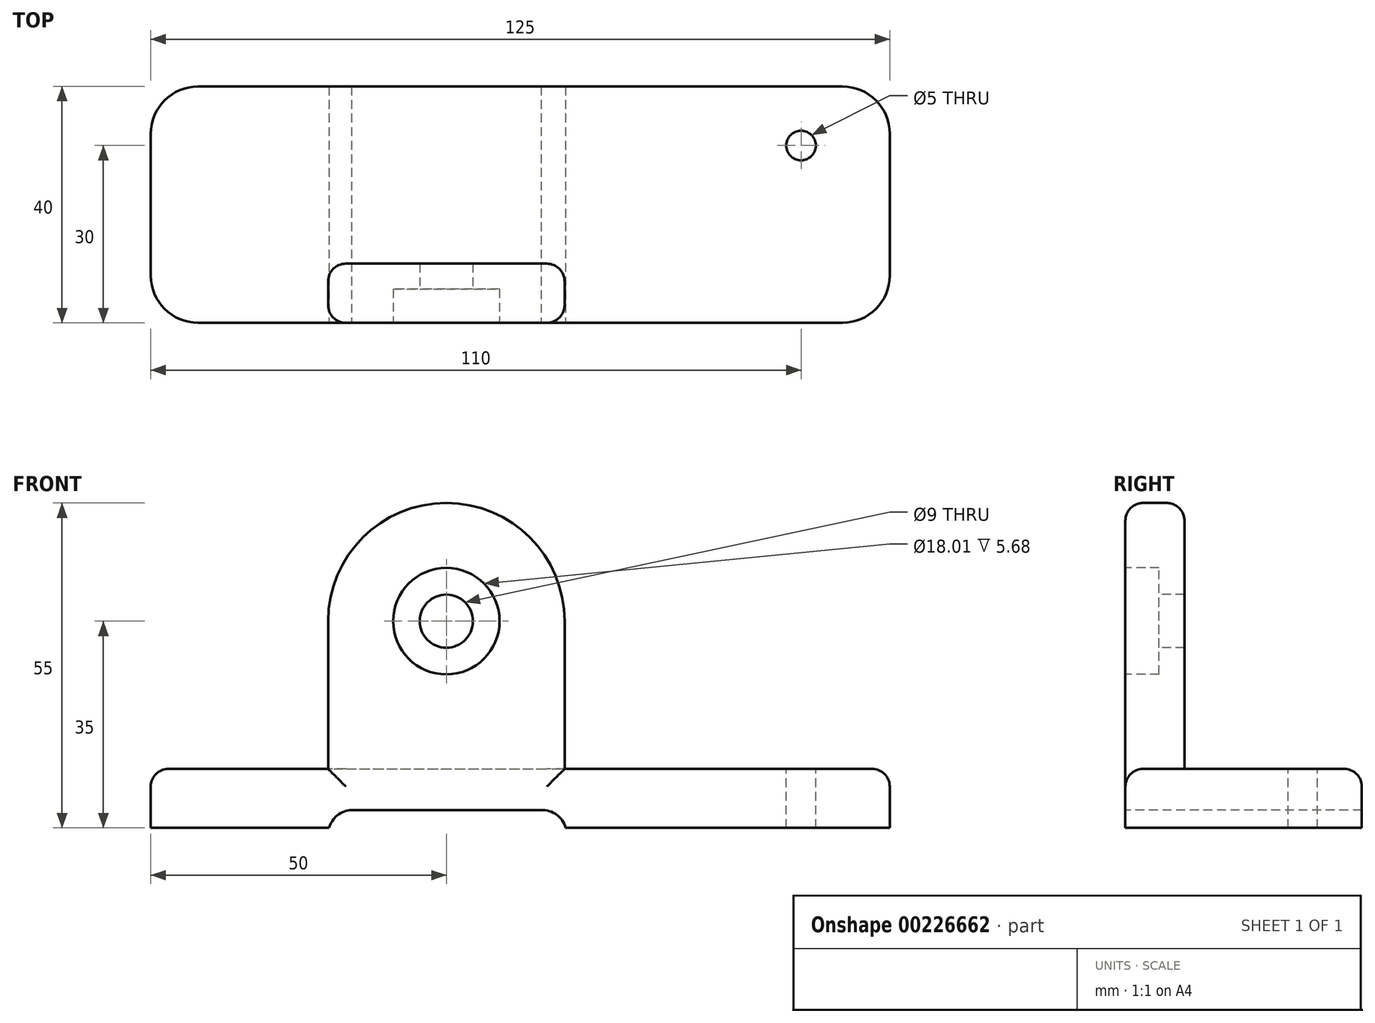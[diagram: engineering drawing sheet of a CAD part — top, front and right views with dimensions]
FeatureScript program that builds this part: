
annotation { "Feature Type Name" : "Feature", "Feature Type Description" : "" }
export const myFeature = defineFeature(function(context is Context, id is Id, definition is map)
    precondition{}
    {
        {
            var Q0;
            Q0=qCreatedBy(makeId("Top.planeOp"),FACE);
            var sketch = newSketch(context, id + "F0", { "sketchPlane" : qUnion([Q0])});
            skLineSegment(sketch, "E0.bottom", {"start": v(-62.5, 20) * mm, "end": v(62.5, 20) * mm});
            skLineSegment(sketch, "E0.top", {"start": v(-62.5, -20) * mm, "end": v(62.5, -20) * mm});
            skLineSegment(sketch, "E0.left", {"start": v(-62.5, 20) * mm, "end": v(-62.5, -20) * mm});
            skLineSegment(sketch, "E0.right", {"start": v(62.5, 20) * mm, "end": v(62.5, -20) * mm});
            skPoint(sketch, "E0.middle", {"position": v(0, 0) * mm});
            skSolve(sketch);
        }
        {
            var Q0;
            Q0=makeQuery(id+"F0.imprint","IMPRINT",FACE,{"disambiguationData":[TD([[makeQuery(id+"F0.imprint","IMPRINT",EDGE,{"derivedFrom":sQuery(id+"F0.wireOp",EDGE,"E0.bottom")}),-1.0]])]});
            extrude(context, id + "F1", {"entities" : qUnion([Q0]), "oppositeDirection" : true, "depth" : 10 * mm});
        }
        {
            var Q0;
            Q0=makeQuery(id+"F1.opExtrude","CAP_FACE",FACE,{"disambiguationData":[OSD([sQuery(id+"F0.wireOp",EDGE,"E0.bottom"),sQuery(id+"F0.wireOp",EDGE,"E0.top"),sQuery(id+"F0.wireOp",EDGE,"E0.left"),sQuery(id+"F0.wireOp",EDGE,"E0.right")])],"isStart":true});
            var sketch = newSketch(context, id + "F2", { "sketchPlane" : qUnion([Q0])});
            skLineSegment(sketch, "E1.bottom", {"start": v(-32.5, -20) * mm, "end": v(7.5, -20) * mm});
            skLineSegment(sketch, "E1.top", {"start": v(-32.5, -10) * mm, "end": v(7.5, -10) * mm});
            skLineSegment(sketch, "E1.left", {"start": v(-32.5, -20) * mm, "end": v(-32.5, -10) * mm});
            skLineSegment(sketch, "E1.right", {"start": v(7.5, -20) * mm, "end": v(7.5, -10) * mm});
            skSolve(sketch);
        }
        {
            var Q0;
            Q0 = qSketchRegion(id + "F2", true);
            extrude(context, id + "F3", {"entities" : qUnion([Q0]), "operationType" : NewBodyOperationType.ADD, "depth" : 25 * mm});
        }
        {
            var Q0;
            Q0=makeQuery(id+"F3.boolean.opBoolean","MERGE",FACE,{"derivedFrom":[makeQuery(id+"F1.opExtrude","SWEPT_FACE",FACE,{"disambiguationData":[OSD([sQuery(id+"F0.wireOp",EDGE,"E0.top")])]}),makeQuery(id+"F3.opExtrude","SWEPT_FACE",FACE,{"disambiguationData":[OSD([sQuery(id+"F2.wireOp",EDGE,"E1.bottom")])]})]});
            var sketch = newSketch(context, id + "F4", { "sketchPlane" : qUnion([Q0])});
            skArc(sketch, "E2", {"start": v(7.5, 25) * mm, "mid": v(-12.5, 45) * mm, "end": v(-32.5, 25) * mm});
            skSolve(sketch);
        }
        {
            var Q0;
            Q0 = qSketchRegion(id + "F4", true);
            var Q1;
            Q1=makeQuery(id+"F4.imprint","IMPRINT",FACE,{"disambiguationData":[TD([[makeQuery(id+"F4.imprint","IMPRINT",EDGE,{"derivedFrom":sQuery(id+"F4.wireOp",EDGE,"E2")}),1.0]])]});
            extrude(context, id + "F5", {"entities" : qUnion([Q0, Q1]), "operationType" : NewBodyOperationType.ADD, "oppositeDirection" : true, "depth" : 10 * mm});
        }
        {
            var Q0;
            {var subQ0=sQuery(id+"F2.wireOp",EDGE,"E1.bottom");Q0=makeQuery(id+"F5.boolean.opBoolean","MERGE",FACE,{"derivedFrom":[makeQuery(id+"F3.boolean.opBoolean","MERGE",FACE,{"derivedFrom":[makeQuery(id+"F1.opExtrude","SWEPT_FACE",FACE,{"disambiguationData":[OSD([sQuery(id+"F0.wireOp",EDGE,"E0.top")])]}),makeQuery(id+"F3.opExtrude","SWEPT_FACE",FACE,{"disambiguationData":[OSD([subQ0])]})]}),makeQuery(id+"F5.opExtrude","CAP_FACE",FACE,{"disambiguationData":[OSD([subQ0,sQuery(id+"F4.wireOp",EDGE,"E2")])],"isStart":true})]});}
            var sketch = newSketch(context, id + "F6", { "sketchPlane" : qUnion([Q0])});
            skCircle(sketch, "E3", {"center": v(-12.5, 25) * mm, "radius": 9 * mm});
            skSolve(sketch);
        }
        {
            var Q0;
            Q0=sQuery(id+"F6.wireOp",VERTEX,"E3.center");
            var Q1;
            Q1=makeQuery(id+"F1.opExtrude","SWEPT_BODY",BODY,{"disambiguationData":[OSD([sQuery(id+"F0.wireOp",EDGE,"E0.bottom"),sQuery(id+"F0.wireOp",EDGE,"E0.top"),sQuery(id+"F0.wireOp",EDGE,"E0.left"),sQuery(id+"F0.wireOp",EDGE,"E0.right")])]});
            hole(context, id + "F7", {"style" : HoleStyle.C_BORE, "endStyle" : HoleEndStyle.THROUGH, "holeDiameter" : 9 * mm, "cBoreDiameter" : 18.01 * mm, "cBoreDepth" : 5.68 * mm, "locations" : qUnion([Q0]), "scope" : qUnion([Q1]), "isTappedThrough" : true});
        }
        {
            var Q0;
            {var subQ0=sQuery(id+"F2.wireOp",EDGE,"E1.bottom");Q0=makeQuery(id+"F5.boolean.opBoolean","MERGE",FACE,{"derivedFrom":[makeQuery(id+"F3.boolean.opBoolean","MERGE",FACE,{"derivedFrom":[makeQuery(id+"F1.opExtrude","SWEPT_FACE",FACE,{"disambiguationData":[OSD([sQuery(id+"F0.wireOp",EDGE,"E0.top")])]}),makeQuery(id+"F3.opExtrude","SWEPT_FACE",FACE,{"disambiguationData":[OSD([subQ0])]})]}),makeQuery(id+"F5.opExtrude","CAP_FACE",FACE,{"disambiguationData":[OSD([subQ0,sQuery(id+"F4.wireOp",EDGE,"E2")])],"isStart":true})]});}
            var sketch = newSketch(context, id + "F8", { "sketchPlane" : qUnion([Q0])});
            skLineSegment(sketch, "E4", {"start": v(-32.33, -10) * mm, "end": v(11.28, -10) * mm, "construction": true});
            skArc(sketch, "E5", {"start": v(-28.55, -7) * mm, "mid": v(-30.94, -7.87) * mm, "end": v(-32.33, -10) * mm});
            skLineSegment(sketch, "E6", {"start": v(11.28, -10) * mm, "end": v(11.28, -10) * mm});
            skLineSegment(sketch, "E7", {"start": v(-28.55, -7) * mm, "end": v(-28.55, -10) * mm, "construction": true});
            skLineSegment(sketch, "E8", {"start": v(3.55, -10) * mm, "end": v(3.55, -7) * mm, "construction": true});
            skArc(sketch, "E9", {"start": v(7.67, -10) * mm, "mid": v(6.15, -7.76) * mm, "end": v(3.55, -7) * mm});
            skLineSegment(sketch, "E10", {"start": v(-28.55, -7) * mm, "end": v(3.55, -7) * mm});
            skPoint(sketch, "E11", {"position": v(-12.5, -7) * mm});
            skSolve(sketch);
        }
        {
            var Q0;
            {var subQ0=sQuery(id+"F8.wireOp",EDGE,"E5");Q0=makeQuery(id+"F8.imprint","IMPRINT",FACE,{"disambiguationData":[TD([[makeQuery(id+"F8.imprint","IMPRINT",EDGE,{"derivedFrom":subQ0}),1.0]])]});}
            extrude(context, id + "F9", {"entities" : qUnion([Q0]), "operationType" : NewBodyOperationType.REMOVE, "endBound" : BoundingType.THROUGH_ALL, "oppositeDirection" : true, "depth" : 25 * mm});
        }
        {
            var Q0;
            Q0=makeQuery(id+"F1.opExtrude","CAP_FACE",FACE,{"disambiguationData":[OSD([sQuery(id+"F0.wireOp",EDGE,"E0.bottom"),sQuery(id+"F0.wireOp",EDGE,"E0.top"),sQuery(id+"F0.wireOp",EDGE,"E0.left"),sQuery(id+"F0.wireOp",EDGE,"E0.right")])],"isStart":true});
            var sketch = newSketch(context, id + "F10", { "sketchPlane" : qUnion([Q0])});
            skCircle(sketch, "E12", {"center": v(47.5, 10) * mm, "radius": 2.5 * mm});
            skSolve(sketch);
        }
        {
            var Q0;
            Q0=makeQuery(id+"F10.imprint","IMPRINT",FACE,{"disambiguationData":[TD([[makeQuery(id+"F10.imprint","IMPRINT",EDGE,{"derivedFrom":sQuery(id+"F10.wireOp",EDGE,"E12")}),1.0]])]});
            extrude(context, id + "F11", {"entities" : qUnion([Q0]), "operationType" : NewBodyOperationType.REMOVE, "endBound" : BoundingType.THROUGH_ALL, "oppositeDirection" : true, "depth" : 25 * mm});
        }
        {
            var Q0;
            Q0=makeQuery(id+"F3.opExtrude","SWEPT_EDGE",EDGE,{"disambiguationData":[OSD([sQuery(id+"F2.wireOp",EDGE,"E1.top"),sQuery(id+"F2.wireOp",EDGE,"E1.right")])]});
            var Q1;
            Q1=makeQuery(id+"F5.opExtrude","CAP_EDGE",EDGE,{"disambiguationData":[OSD([sQuery(id+"F4.wireOp",EDGE,"E2")])],"isStart":true});
            fillet(context, id + "F12", {"entities" : qUnion([Q0, Q1]), "radius" : 3 * mm, "tangentPropagation" : true, "allowEdgeOverflow" : false});
        }
        {
            var Q0;
            {var subQ0=sQuery(id+"F0.wireOp",EDGE,"E0.right");var subQ1=sQuery(id+"F0.wireOp",EDGE,"E0.top");Q0=makeQuery(id+"F3.boolean.opBoolean","SPLIT",EDGE,{"disambiguationData":[TD([makeQuery(id+"F1.opExtrude","SWEPT_FACE",FACE,{"disambiguationData":[OSD([subQ0])]})])],"derivedFrom":makeQuery(id+"F1.opExtrude","CAP_EDGE",EDGE,{"disambiguationData":[OSD([subQ1])],"isStart":true})});}
            var Q1;
            Q1=makeQuery(id+"F1.opExtrude","CAP_EDGE",EDGE,{"disambiguationData":[OSD([sQuery(id+"F0.wireOp",EDGE,"E0.right")])],"isStart":true});
            var Q2;
            {var subQ0=sQuery(id+"F0.wireOp",EDGE,"E0.left");var subQ1=sQuery(id+"F0.wireOp",EDGE,"E0.top");Q2=makeQuery(id+"F3.boolean.opBoolean","SPLIT",EDGE,{"disambiguationData":[TD([makeQuery(id+"F1.opExtrude","SWEPT_FACE",FACE,{"disambiguationData":[OSD([subQ0])]})])],"derivedFrom":makeQuery(id+"F1.opExtrude","CAP_EDGE",EDGE,{"disambiguationData":[OSD([subQ1])],"isStart":true})});}
            var Q3;
            Q3=makeQuery(id+"F1.opExtrude","CAP_EDGE",EDGE,{"disambiguationData":[OSD([sQuery(id+"F0.wireOp",EDGE,"E0.left")])],"isStart":true});
            var Q4;
            Q4=makeQuery(id+"F1.opExtrude","CAP_EDGE",EDGE,{"disambiguationData":[OSD([sQuery(id+"F0.wireOp",EDGE,"E0.bottom")])],"isStart":true});
            var Q5;
            Q5=makeQuery(id+"F3.opExtrude","CAP_EDGE",EDGE,{"disambiguationData":[OSD([sQuery(id+"F2.wireOp",EDGE,"E1.right")])],"isStart":true});
            fillet(context, id + "F13", {"entities" : qUnion([Q0, Q1, Q2, Q3, Q4, Q5]), "radius" : 3 * mm, "tangentPropagation" : true, "allowEdgeOverflow" : false});
        }
        {
            var Q0;
            Q0=makeQuery(id+"F1.opExtrude","SWEPT_EDGE",EDGE,{"disambiguationData":[OSD([sQuery(id+"F0.wireOp",EDGE,"E0.bottom"),sQuery(id+"F0.wireOp",EDGE,"E0.right")])]});
            var Q1;
            Q1=makeQuery(id+"F1.opExtrude","SWEPT_EDGE",EDGE,{"disambiguationData":[OSD([sQuery(id+"F0.wireOp",EDGE,"E0.top"),sQuery(id+"F0.wireOp",EDGE,"E0.right")])]});
            var Q2;
            Q2=makeQuery(id+"F1.opExtrude","SWEPT_EDGE",EDGE,{"disambiguationData":[OSD([sQuery(id+"F0.wireOp",EDGE,"E0.bottom"),sQuery(id+"F0.wireOp",EDGE,"E0.left")])]});
            var Q3;
            Q3=makeQuery(id+"F1.opExtrude","SWEPT_EDGE",EDGE,{"disambiguationData":[OSD([sQuery(id+"F0.wireOp",EDGE,"E0.top"),sQuery(id+"F0.wireOp",EDGE,"E0.left")])]});
            fillet(context, id + "F14", {"entities" : qUnion([Q0, Q1, Q2, Q3]), "radius" : 8 * mm, "tangentPropagation" : true, "allowEdgeOverflow" : false});
        }
    });
